# Revit family: Lavatory_Toilet-Combination-Ligature_Resistant-Acorn-Secur_Care-LR1452FA
name_source: partatom
category: Plumbing Fixtures
units: mm (PartAtom-declared; Revit-internal decimal feet)

## family parameters
Cut with Voids When Loaded = No
Host = Face
OmniClass Number = 23.45.05.14.31
OmniClass Title = Combination Toilets
Part Type = Normal
Room Calculation Point = No
Round Connector Dimension = Use Diameter
Shared = Yes

## types (1)
- LR1452FA-RO-2-DMB-PBH-03-M-EVSFV-1.28 GPF
    -LR-DMF -PBH Ligature Resistant Cup Filler & Hemispherical Pushbutton = Yes
    03-M - Air-Control, Single Temp, Metering = Yes
    04-M - Air-Control, H&C, Metering = No
    1.28 GPF (HET) = Yes
    2 - On-Floor, Wall Outlet = Yes
    3 - On-Floor, Floor Outlet = No
    42" Long Grab Bar by others = Yes
    ADA Compliant = Yes
    Assembly Code = D2010
    BRS - Brass Body Valve = No
    CI - Cycle Interrupt for Time-Trol Valves = No
    CW - Combined Waste = No
    CW Connection = Yes
    CWFU = 5
    Compliance Certifications = CBC (California Title 24), ASME A112.19.3 and CSA B45.4, ANSI A117.1, Public Law 111-380 (NO-LEAD), CHSC 116875 and NSF/ANSI/CAN 61-2020  Section 9
    DMB Deck Mounted Hemispherical Bubbler & -04 Pushbuttons = Yes
    Default Elevation = 0"
    Description = Secur-Care - Ligature Resistant LR1452FA Series CBC (California Title 24) - Compliant - Ligature Resistant Lav/Toilet Comby Offset Toilet Bowl - Front Access
    EGE Enviro-Glaze Color Specify: Toilet Exterior Only = No
    EVS1 - Electronic Valve System - Single Temp = No
    EVS2 - Electronic Valve System - Hot & Cold = No
    EVSFV - Electronic Flush Valve = Yes
    EVSP1 - Electronic Valve System w/ Piezo Pushbutton = No
    EVSP2 - Electronic Valve System w/ Piezo Pushbuttons = No
    EVSPFV - Electronic Flush Valve w/ Piezo Pushbutton = No
    FT - Flood-Trol = No
    FTA - Flood-Trol, Auto-Reset = No
    FTE - Flood-Trol, Electronic = No
    FVBO - Flush Valve by Others = No
    FVH - Flush Valve, Hydraulic = No
    Finish = Stainless Steel-Acorn-304-Satin
    Flow Rate = 25 PSI flow pressure when used in conjunction with a minimum of 1.28 GPF
    Flush Mounted Access Panels = Yes
    Flush Valve Inlet Height = 22 1/2"
    Grab Bar Length = 50 3/8"
    Grab Bar w/ L shaped closure plate = Yes
    HET - High Efficiency Toilet Design = No
    HPS - High Polish Seat #7 Finish = No
    HW Connection = No
    HWFU = 0
    Height = 33 1/4"
    Hydraulic Flush Pushbuttons = Yes
    Inlet Diameter Connection = 1/2"
    Installation Instruction Link = https://www.acorneng.com
    LGB - Less Grab Bar = No
    LO - Left Offset = No
    LPFV - Less Punching For Flush Valve = No
    Lavatory Outlet Connection Height = 24 3/4"
    Ligature Resistant Skirt = Yes
    MA - Manifolded Valve (Specify Unit) = No
    MT - Metal Template (Only 1 Required Per Project) = No
    MTP1 - Single Temp = No
    MTP2 - Hot & Cold = No
    MTPFV Master-Trol PLUS Electronic Flush Valve = No
    MTPP1 - Single Temp, Piezo Button = No
    MTPP2 - Hot & Cold, Piezo Buttons = No
    MTPPFV Master-Trol PLUS Electronic Flush Valve w/ Piezo = No
    MVC1 - Time-Trol - Single Temp = No
    MVC1-BAT - Time-Trol - Single Temp, Battery Operated = No
    MVC2 - Time-Trol - Hot & Cold = No
    MVC2-BAT - Time-Trol - Hot & Cold, Battery Operated = No
    MVCFV - Time-Trol Electronic Flush Valve = No
    Manufacturer = Acorn Engineering
    Material = Stainless Steel-Acorn-304-Satin
    Model = LR1452FA-RO-2-DMB-PBH-03-M-EVSFV-1.28 GPF
    Overall Height = 37 1/2"
    PE - Plain End Toilet Waste 2-3/8" in lieu of Standard Gasket = No
    PFB - Power Failure Bypass (Provides drinking water in the event of power failure) = No
    PH - Paper Holder Same Side As Toilet = No
    PPZ1 - Programmable Piezo Pushbutton (Single Temperature Only) = No
    PPZ2 - Programmable Piezo Button (Hot and Cold) = No
    Product Documentation Link = https://www.acorneng.com
    Product Page URL = https://www.acorneng.com
    RO - Right Offset = Yes
    SW - Wall Sleeve = No
    TB - Double Toothbrush Holder (Lavy Housing Opposite Grab Bar) = No
    TB - Single Toothbrush Holder (Lavy Housing Opposite Grab Bar) = No
    TF - 120VAC to 24VAC Transformer = No
    TG - 12 Gage (2.77mm) Cabinet = No
    TH - Double Towel Hook On Lavy Side = No
    TH - Single Towel Hook On Lavy Side = No
    TSC - Toilet Shipping Cover = No
    TWE - 3" (76mm) Standard Toilet Waste Extension (Specify Length Beyond Fixture) = No
    Toilet Height = 18"
    URL = http://www.acorneng.com
    Vent Connection = No
    WFU = 5
    WO3 - 3" Toilet P-Trap (3.5 GPF Only) = No
    WO3B - 3" (76mm) Bell Waste Outlet = No
    Wall Anchors = Yes
    Waste 1 Connection Height = 14 1/4"
    Waste Connection = Yes
    Waste Connection Diameter = 2 3/8"
    Width = 52 1/4"

## geometry (parser evidence)
native form markers: Sweep x4
no freeform markers — native parametric forms only
